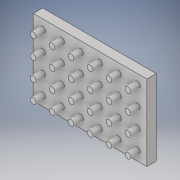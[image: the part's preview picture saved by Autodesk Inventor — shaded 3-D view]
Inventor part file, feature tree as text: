
AUTODESK INVENTOR PART (.ipt)
format: ipt  version: 2018 (Build 220112000, 112)  size: 148,992 bytes
history: native  units: in
note: dims shown in document units (in); Inventor stores cm internally (conversion verified against a paired STEP export)
features: extrude x2, sketch x2, pattern_linear x1
ambient origin geometry x8: Origin, YZ Plane, XZ Plane, XY Plane, X Axis, Y Axis, Z Axis, Center Point
bodies: Solid1 (feature_tree)
feature tree (5):
  extrude  "Extrusion1"  Depth=4.0in
  extrude  "Extrusion2"  Depth=1.0in
  pattern_linear  "Rectangular Pattern1"  Spacing1=0.5in  [1 undecoded]
  sketch  "Sketch1"  dims[d0=6.0in d1=4.0in]
  sketch  "Sketch2"  dims[d2=0.5in d3=0.0in d4=0.3in d5=0.5in d6=0.5in d7=0.5in d8=0.0in d9=1.5748in d11=1.0in d12=2.3622in d14=1.0in]
note: 1 required parameter value undecoded (feature->parameter linkage not recoverable at this tier; creation-order binding heuristic only, values carry confidence <= 0.55)
